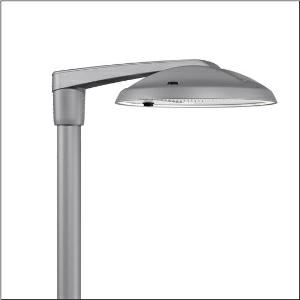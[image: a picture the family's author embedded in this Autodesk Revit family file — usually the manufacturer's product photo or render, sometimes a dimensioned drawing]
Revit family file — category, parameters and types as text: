
# Revit family: dl_r__50_iq_mini___st1_0a_5xa248d31y08ne_98a7
name_source: partatom
category: Lighting Fixtures
units: mm (PartAtom-declared; Revit-internal decimal feet)

## family parameters
Cut with Voids When Loaded = No
Host = Face
Light Source = No
Part Type = Normal
Room Calculation Point = No
Round Connector Dimension = Use Diameter
Shared = No

## types (1)
- --- (1 x LED, 17900 lm, 110.1 W, 3000K)
    Apparent Load = 110 VA
    CIE Flux Codes = 37 72 97 100 100
    Color Rendering = 70
    Color Temperature = 3000K
    Default Elevation = 1800 mm
    Description = DL® 50 iQ mini, mast luminaire, primary light control with lens, of PMMA, primary optical cover: cover, of toughened safety glass, transparent, light distribution: ST1.0a, light emission: direct distribution, primary light characteristic: asymmetric, installation type: post-top, side-entry, LED, High Power LED, rated luminous flux: 17.900lm, luminous efficacy: 163lm/W, light colour: 730, colour temperature: 3000K, control: optimised constant luminous flux control (CLO 2.0), Desk-Remote (wireless, voltage-free reading and setting of iQ features in the workshop via application-optimized NFC function/RFID function), Light-Fading, Smart-Wire, Night-Set, Lumen-Switch, Temp-Guard, Auto-Match, Street-Remote, presetting dimming logarithmic, mains connection: 230..240V, AC, 50/60Hz, connection cable pre-assembled, cable length: 10,5m, start of lifetime: 110W, end of service life: 116W, reduction: 50W, luminaire housing, of diecast aluminium, powder-coated, Siteco® metallic grey (DB 702S), inclination adjustable: 0°, 5°, 10° (post-top) | 0°, -5°, -10°, -15° (side-entry), please order mast post-top element or mast side-entry element separately, diameter: 500mm, height: 115mm, post-top: for spigot size d x l = 76 x 100mm; with reducer (optional accessory) 60 x 100mm | side-entry: for spigot size d x l = 60 x 100mm; with reducer (optional accessory) 42 x 100mm, Smart Interface below and above, protection rating (complete): IP66, insulation class (complete): insulation class II (safety insulation), certification: CE, ENEC, VDE, impact resistance: IK08, permissible operating ambient temperature for outdoor applications: -25..+40°C, standard-compliant lighting for roads and squares, packaging unit: 1 piece

Light Distribution: ST1.0a
    Height = 115 mm
    Lamp = 1 x LED
    Lamp Light Flux = 17900 lm
    Lamp Power = 110.1 W
    Lamp count = 1
    Length = 500 mm
    Luminous efficacy = 163 lm/W
    Manufacturer = Siteco
    ModVariant = No
    Model = 5XA248D31Y08NE
    Number of Poles = 1
    OnlyDefault = Yes
    Power Factor = 1
    Product Name = DL® 50 iQ mini | ST1.0a
    Product group = mast luminaire | pylon top
    ProductGroupID = 6100
    Protection Class = Protection class II
    Protection Degree = IP 66
    RLX_Detail_Level = 1
    RLX_Emergency_Light_Flux = 0 lm
    RLX_Emergency_Type = 0
    RLX_Emergency_Type_DB = No
    RlxData = <blob elided: 106989 chars, md5=d00e006e>
    Socket = socket
    Standby Power = 0 W
    System Light Flux = 17900 lm
    System Power = 110 W
    Type Comments = factory setting: luminous flux: 100 % | dim-lin: 254 | 601 mA
    Type Image = l_1251786.jpg
    URL = http://relux.com
    VarID = @adj_005693
    Voltage = 0 V
    Weight = 0.00 kg
    Width = 0 mm  [stored 0 ft]

note: [stored X ft] marks values corroborated as IEEE doubles in the binary element streams (Revit-internal decimal feet)

## geometry (parser evidence)
native form markers: Blend x4, Sweep x10
no freeform markers — native parametric forms only
